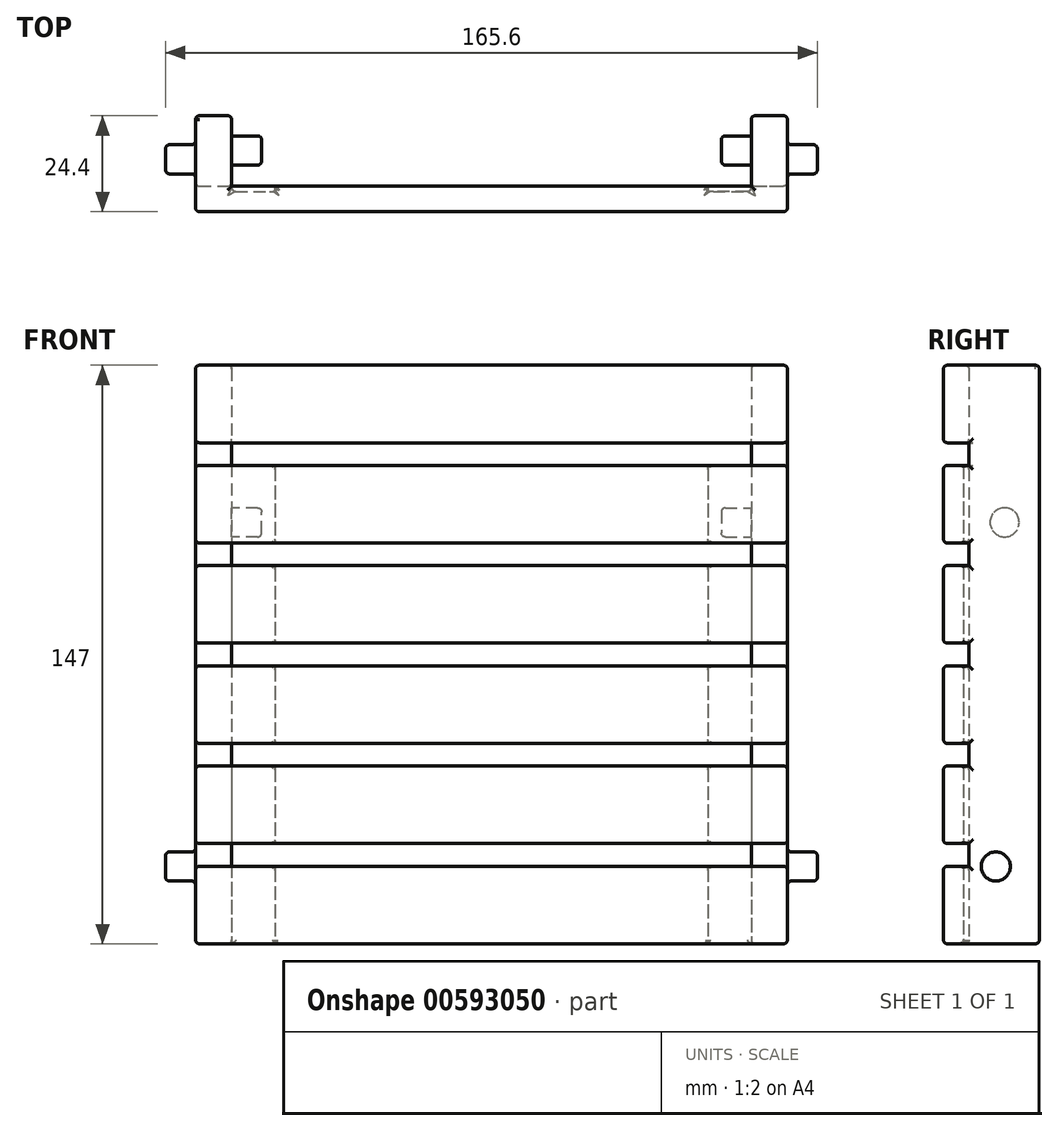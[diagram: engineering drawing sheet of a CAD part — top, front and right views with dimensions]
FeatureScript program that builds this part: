
annotation { "Feature Type Name" : "Feature", "Feature Type Description" : "" }
export const myFeature = defineFeature(function(context is Context, id is Id, definition is map)
    precondition{}
    {
        {
            var Q0;
            Q0=qCreatedBy(makeId("Front.planeOp"),FACE);
            var sketch = newSketch(context, id + "F0", { "sketchPlane" : qUnion([Q0])});
            skLineSegment(sketch, "E0.bottom", {"start": v(-75.2, 73.5) * mm, "end": v(-66, 73.5) * mm});
            skLineSegment(sketch, "E0.top", {"start": v(-75.2, -73.5) * mm, "end": v(-66, -73.5) * mm});
            skLineSegment(sketch, "E0.left", {"start": v(-75.2, 73.5) * mm, "end": v(-75.2, -73.5) * mm});
            skLineSegment(sketch, "E0.right", {"start": v(-66, 73.5) * mm, "end": v(-66, -73.5) * mm});
            skLineSegment(sketch, "E1.MirrorCS", {"start": v(75.2, 73.5) * mm, "end": v(66, 73.5) * mm});
            skLineSegment(sketch, "E2.MirrorCS", {"start": v(75.2, -73.5) * mm, "end": v(66, -73.5) * mm});
            skLineSegment(sketch, "E3.MirrorCS", {"start": v(66, 73.5) * mm, "end": v(66, -73.5) * mm});
            skLineSegment(sketch, "E4.MirrorCS", {"start": v(75.2, 73.5) * mm, "end": v(75.2, -73.5) * mm});
            skSolve(sketch);
        }
        {
            var Q0;
            Q0=qSketchRegion(id+"F0",true);
            extrude(context, id + "F1", {"entities" : qUnion([Q0]), "depth" : 17.9 * mm});
        }
        {
            var Q0;
            Q0=makeQuery(id+"F1.opExtrude","CAP_FACE",FACE,{"disambiguationData":[OSD([sQuery(id+"F0.wireOp",EDGE,"E0.bottom"),sQuery(id+"F0.wireOp",EDGE,"E0.top"),sQuery(id+"F0.wireOp",EDGE,"E0.left"),sQuery(id+"F0.wireOp",EDGE,"E0.right")])],"isStart":false});
            var sketch = newSketch(context, id + "F2", { "sketchPlane" : qUnion([Q0])});
            skLineSegment(sketch, "E5.bottom", {"start": v(-75.2, 73.5) * mm, "end": v(75.2, 73.5) * mm});
            skLineSegment(sketch, "E5.top", {"start": v(-75.2, 53.8) * mm, "end": v(75.2, 53.8) * mm});
            skLineSegment(sketch, "E5.left", {"start": v(-75.2, 73.5) * mm, "end": v(-75.2, 53.8) * mm});
            skLineSegment(sketch, "E5.right", {"start": v(75.2, 73.5) * mm, "end": v(75.2, 53.8) * mm});
            skLineSegment(sketch, "E6.bottom", {"start": v(-75.2, 48.04) * mm, "end": v(75.2, 48.04) * mm});
            skLineSegment(sketch, "E6.top", {"start": v(-75.2, 28.34) * mm, "end": v(75.2, 28.34) * mm});
            skLineSegment(sketch, "E6.left", {"start": v(-75.2, 48.04) * mm, "end": v(-75.2, 28.34) * mm});
            skLineSegment(sketch, "E6.right", {"start": v(75.2, 48.04) * mm, "end": v(75.2, 28.34) * mm});
            skLineSegment(sketch, "E7.bottom", {"start": v(-75.2, 22.58) * mm, "end": v(75.2, 22.58) * mm});
            skLineSegment(sketch, "E7.top", {"start": v(-75.2, 2.88) * mm, "end": v(75.2, 2.88) * mm});
            skLineSegment(sketch, "E7.left", {"start": v(-75.2, 22.58) * mm, "end": v(-75.2, 2.88) * mm});
            skLineSegment(sketch, "E7.right", {"start": v(75.2, 22.58) * mm, "end": v(75.2, 2.88) * mm});
            skLineSegment(sketch, "E8.bottom", {"start": v(-75.2, -2.88) * mm, "end": v(75.2, -2.88) * mm});
            skLineSegment(sketch, "E8.top", {"start": v(-75.2, -22.58) * mm, "end": v(75.2, -22.58) * mm});
            skLineSegment(sketch, "E8.left", {"start": v(-75.2, -2.88) * mm, "end": v(-75.2, -22.58) * mm});
            skLineSegment(sketch, "E8.right", {"start": v(75.2, -2.88) * mm, "end": v(75.2, -22.58) * mm});
            skLineSegment(sketch, "E9.bottom", {"start": v(-75.2, -28.34) * mm, "end": v(75.2, -28.34) * mm});
            skLineSegment(sketch, "E9.top", {"start": v(-75.2, -48.04) * mm, "end": v(75.2, -48.04) * mm});
            skLineSegment(sketch, "E9.left", {"start": v(-75.2, -28.34) * mm, "end": v(-75.2, -48.04) * mm});
            skLineSegment(sketch, "E9.right", {"start": v(75.2, -28.34) * mm, "end": v(75.2, -48.04) * mm});
            skLineSegment(sketch, "E10.bottom", {"start": v(-75.2, -53.8) * mm, "end": v(75.2, -53.8) * mm});
            skLineSegment(sketch, "E10.top", {"start": v(-75.2, -73.5) * mm, "end": v(75.2, -73.5) * mm});
            skLineSegment(sketch, "E10.left", {"start": v(-75.2, -53.8) * mm, "end": v(-75.2, -73.5) * mm});
            skLineSegment(sketch, "E10.right", {"start": v(75.2, -53.8) * mm, "end": v(75.2, -73.5) * mm});
            skSolve(sketch);
        }
        {
            var Q0;
            Q0=qSketchRegion(id+"F2",true);
            extrude(context, id + "F3", {"entities" : qUnion([Q0]), "depth" : 6.5 * mm});
        }
        {
            var Q0;
            Q0=makeQuery(id+"F1.opExtrude","SWEPT_BODY",BODY,{"disambiguationData":[OSD([sQuery(id+"F0.wireOp",EDGE,"E0.bottom"),sQuery(id+"F0.wireOp",EDGE,"E0.top"),sQuery(id+"F0.wireOp",EDGE,"E0.left"),sQuery(id+"F0.wireOp",EDGE,"E0.right")])]});
            var Q1;
            Q1=makeQuery(id+"F1.opExtrude","SWEPT_BODY",BODY,{"disambiguationData":[OSD([sQuery(id+"F0.wireOp",EDGE,"E1.MirrorCS"),sQuery(id+"F0.wireOp",EDGE,"E2.MirrorCS"),sQuery(id+"F0.wireOp",EDGE,"E3.MirrorCS"),sQuery(id+"F0.wireOp",EDGE,"E4.MirrorCS")])]});
            var Q2;
            Q2=makeQuery(id+"F3.opExtrude","SWEPT_BODY",BODY,{"disambiguationData":[OSD([sQuery(id+"F2.wireOp",EDGE,"E5.bottom"),sQuery(id+"F2.wireOp",EDGE,"E5.top"),sQuery(id+"F2.wireOp",EDGE,"E5.left"),sQuery(id+"F2.wireOp",EDGE,"E5.right")])]});
            var Q3;
            Q3=makeQuery(id+"F3.opExtrude","SWEPT_BODY",BODY,{"disambiguationData":[OSD([sQuery(id+"F2.wireOp",EDGE,"E6.bottom"),sQuery(id+"F2.wireOp",EDGE,"E6.top"),sQuery(id+"F2.wireOp",EDGE,"E6.left"),sQuery(id+"F2.wireOp",EDGE,"E6.right")])]});
            var Q4;
            Q4=makeQuery(id+"F3.opExtrude","SWEPT_BODY",BODY,{"disambiguationData":[OSD([sQuery(id+"F2.wireOp",EDGE,"E7.bottom"),sQuery(id+"F2.wireOp",EDGE,"E7.top"),sQuery(id+"F2.wireOp",EDGE,"E7.left"),sQuery(id+"F2.wireOp",EDGE,"E7.right")])]});
            var Q5;
            Q5=makeQuery(id+"F3.opExtrude","SWEPT_BODY",BODY,{"disambiguationData":[OSD([sQuery(id+"F2.wireOp",EDGE,"E8.bottom"),sQuery(id+"F2.wireOp",EDGE,"E8.top"),sQuery(id+"F2.wireOp",EDGE,"E8.left"),sQuery(id+"F2.wireOp",EDGE,"E8.right")])]});
            var Q6;
            Q6=makeQuery(id+"F3.opExtrude","SWEPT_BODY",BODY,{"disambiguationData":[OSD([sQuery(id+"F2.wireOp",EDGE,"E9.bottom"),sQuery(id+"F2.wireOp",EDGE,"E9.top"),sQuery(id+"F2.wireOp",EDGE,"E9.left"),sQuery(id+"F2.wireOp",EDGE,"E9.right")])]});
            var Q7;
            Q7=makeQuery(id+"F3.opExtrude","SWEPT_BODY",BODY,{"disambiguationData":[OSD([sQuery(id+"F2.wireOp",EDGE,"E10.bottom"),sQuery(id+"F2.wireOp",EDGE,"E10.top"),sQuery(id+"F2.wireOp",EDGE,"E10.left"),sQuery(id+"F2.wireOp",EDGE,"E10.right")])]});
            booleanBodies(context, id + "F4", {"operationType" : BooleanOperationType.UNION, "tools" : qUnion([Q0, Q1, Q2, Q3, Q4, Q5, Q6, Q7])});
        }
        {
            var Q0;
            Q0=makeQuery(id+"F4.opBoolean","MERGE",FACE,{"derivedFrom":[makeQuery(id+"F1.opExtrude","SWEPT_FACE",FACE,{"disambiguationData":[OSD([sQuery(id+"F0.wireOp",EDGE,"E0.left")])]}),makeQuery(id+"F3.opExtrude","SWEPT_FACE",FACE,{"disambiguationData":[OSD([sQuery(id+"F2.wireOp",EDGE,"E5.left")])]}),makeQuery(id+"F3.opExtrude","SWEPT_FACE",FACE,{"disambiguationData":[OSD([sQuery(id+"F2.wireOp",EDGE,"E6.left")])]}),makeQuery(id+"F3.opExtrude","SWEPT_FACE",FACE,{"disambiguationData":[OSD([sQuery(id+"F2.wireOp",EDGE,"E7.left")])]}),makeQuery(id+"F3.opExtrude","SWEPT_FACE",FACE,{"disambiguationData":[OSD([sQuery(id+"F2.wireOp",EDGE,"E8.left")])]}),makeQuery(id+"F3.opExtrude","SWEPT_FACE",FACE,{"disambiguationData":[OSD([sQuery(id+"F2.wireOp",EDGE,"E9.left")])]}),makeQuery(id+"F3.opExtrude","SWEPT_FACE",FACE,{"disambiguationData":[OSD([sQuery(id+"F2.wireOp",EDGE,"E10.left")])]})]});
            var sketch = newSketch(context, id + "F5", { "sketchPlane" : qUnion([Q0])});
            skCircle(sketch, "E11", {"center": v(11.08, -53.85) * mm, "radius": 3.7 * mm});
            skSolve(sketch);
        }
        {
            var Q0;
            Q0=makeQuery(id+"F5.imprint","IMPRINT",FACE,{"disambiguationData":[TD([[makeQuery(id+"F5.imprint","IMPRINT",EDGE,{"derivedFrom":sQuery(id+"F5.wireOp",EDGE,"E11")}),1.0]])]});
            extrude(context, id + "F6", {"entities" : qUnion([Q0]), "operationType" : NewBodyOperationType.ADD, "depth" : 7.6 * mm});
        }
        {
            var Q0;
            Q0=makeQuery(id+"F4.opBoolean","MERGE",FACE,{"derivedFrom":[makeQuery(id+"F1.opExtrude","SWEPT_FACE",FACE,{"disambiguationData":[OSD([sQuery(id+"F0.wireOp",EDGE,"E4.MirrorCS")])]}),makeQuery(id+"F3.opExtrude","SWEPT_FACE",FACE,{"disambiguationData":[OSD([sQuery(id+"F2.wireOp",EDGE,"E5.right")])]}),makeQuery(id+"F3.opExtrude","SWEPT_FACE",FACE,{"disambiguationData":[OSD([sQuery(id+"F2.wireOp",EDGE,"E6.right")])]}),makeQuery(id+"F3.opExtrude","SWEPT_FACE",FACE,{"disambiguationData":[OSD([sQuery(id+"F2.wireOp",EDGE,"E7.right")])]}),makeQuery(id+"F3.opExtrude","SWEPT_FACE",FACE,{"disambiguationData":[OSD([sQuery(id+"F2.wireOp",EDGE,"E8.right")])]}),makeQuery(id+"F3.opExtrude","SWEPT_FACE",FACE,{"disambiguationData":[OSD([sQuery(id+"F2.wireOp",EDGE,"E9.right")])]}),makeQuery(id+"F3.opExtrude","SWEPT_FACE",FACE,{"disambiguationData":[OSD([sQuery(id+"F2.wireOp",EDGE,"E10.right")])]})]});
            var sketch = newSketch(context, id + "F7", { "sketchPlane" : qUnion([Q0])});
            skCircle(sketch, "E12", {"center": v(-11.08, -53.85) * mm, "radius": 3.7 * mm});
            skSolve(sketch);
        }
        {
            var Q0;
            Q0=makeQuery(id+"F7.imprint","IMPRINT",FACE,{"disambiguationData":[TD([[makeQuery(id+"F7.imprint","IMPRINT",EDGE,{"derivedFrom":sQuery(id+"F7.wireOp",EDGE,"E12")}),1.0]])]});
            extrude(context, id + "F8", {"entities" : qUnion([Q0]), "operationType" : NewBodyOperationType.ADD, "depth" : 7.6 * mm});
        }
        {
            var Q0;
            Q0=makeQuery(id+"F1.opExtrude","SWEPT_FACE",FACE,{"disambiguationData":[OSD([sQuery(id+"F0.wireOp",EDGE,"E3.MirrorCS")])]});
            var sketch = newSketch(context, id + "F9", { "sketchPlane" : qUnion([Q0])});
            skCircle(sketch, "E13", {"center": v(8.84, 33.58) * mm, "radius": 3.7 * mm});
            skSolve(sketch);
        }
        {
            var Q0;
            Q0=makeQuery(id+"F9.imprint","IMPRINT",FACE,{"disambiguationData":[TD([[makeQuery(id+"F9.imprint","IMPRINT",EDGE,{"derivedFrom":sQuery(id+"F9.wireOp",EDGE,"E13")}),1.0]])]});
            extrude(context, id + "F10", {"entities" : qUnion([Q0]), "operationType" : NewBodyOperationType.ADD, "depth" : 7.6 * mm});
        }
        {
            var Q0;
            Q0=makeQuery(id+"F1.opExtrude","SWEPT_FACE",FACE,{"disambiguationData":[OSD([sQuery(id+"F0.wireOp",EDGE,"E0.right")])]});
            var sketch = newSketch(context, id + "F11", { "sketchPlane" : qUnion([Q0])});
            skCircle(sketch, "E14", {"center": v(-8.84, 33.58) * mm, "radius": 3.7 * mm});
            skSolve(sketch);
        }
        {
            var Q0;
            Q0=makeQuery(id+"F11.imprint","IMPRINT",FACE,{"disambiguationData":[TD([[makeQuery(id+"F11.imprint","IMPRINT",EDGE,{"derivedFrom":sQuery(id+"F11.wireOp",EDGE,"E14")}),1.0]])]});
            extrude(context, id + "F12", {"entities" : qUnion([Q0]), "operationType" : NewBodyOperationType.ADD, "depth" : 7.6 * mm});
        }
        {
            var Q0;
            Q0=makeQuery(id+"F3.opExtrude","CAP_FACE",FACE,{"disambiguationData":[OSD([sQuery(id+"F2.wireOp",EDGE,"E6.bottom"),sQuery(id+"F2.wireOp",EDGE,"E6.top"),sQuery(id+"F2.wireOp",EDGE,"E6.left"),sQuery(id+"F2.wireOp",EDGE,"E6.right")])],"isStart":true});
            var sketch = newSketch(context, id + "F13", { "sketchPlane" : qUnion([Q0])});
            skLineSegment(sketch, "E15.bottom", {"start": v(-66, 48.04) * mm, "end": v(-55, 48.04) * mm});
            skLineSegment(sketch, "E15.top", {"start": v(-66, -73.5) * mm, "end": v(-55, -73.5) * mm});
            skLineSegment(sketch, "E15.left", {"start": v(-66, 48.04) * mm, "end": v(-66, -73.5) * mm});
            skLineSegment(sketch, "E15.right", {"start": v(-55, 48.04) * mm, "end": v(-55, -73.5) * mm});
            skLineSegment(sketch, "E16.bottom", {"start": v(66, 48.04) * mm, "end": v(55, 48.04) * mm});
            skLineSegment(sketch, "E16.top", {"start": v(66, -73.5) * mm, "end": v(55, -73.5) * mm});
            skLineSegment(sketch, "E16.left", {"start": v(66, 48.04) * mm, "end": v(66, -73.5) * mm});
            skLineSegment(sketch, "E16.right", {"start": v(55, 48.04) * mm, "end": v(55, -73.5) * mm});
            skSolve(sketch);
        }
        {
            var Q0;
            {var subQ0=sQuery(id+"F13.wireOp",EDGE,"E15.top");Q0=makeQuery(id+"F13.imprint","IMPRINT",FACE,{"disambiguationData":[TD([[makeQuery(id+"F13.imprint","IMPRINT",EDGE,{"derivedFrom":subQ0}),1.0]])]});}
            var Q1;
            {var subQ0=sQuery(id+"F13.wireOp",EDGE,"E15.bottom");Q1=makeQuery(id+"F13.imprint","IMPRINT",FACE,{"disambiguationData":[TD([[makeQuery(id+"F13.imprint","IMPRINT",EDGE,{"derivedFrom":subQ0}),1.0]])]});}
            var Q2;
            {var subQ0=sQuery(id+"F13.wireOp",EDGE,"E16.bottom");Q2=makeQuery(id+"F13.imprint","IMPRINT",FACE,{"disambiguationData":[TD([[makeQuery(id+"F13.imprint","IMPRINT",EDGE,{"derivedFrom":subQ0}),1.0]])]});}
            var Q3;
            {var subQ0=sQuery(id+"F13.wireOp",EDGE,"E16.top");Q3=makeQuery(id+"F13.imprint","IMPRINT",FACE,{"disambiguationData":[TD([[makeQuery(id+"F13.imprint","IMPRINT",EDGE,{"derivedFrom":subQ0}),-1.0]])]});}
            extrude(context, id + "F14", {"entities" : qUnion([Q0, Q1, Q2, Q3]), "operationType" : NewBodyOperationType.REMOVE, "oppositeDirection" : true, "depth" : 1.35 * mm});
        }
        {
            var Q0;
            Q0=makeQuery(id+"F3.opExtrude","CAP_FACE",FACE,{"disambiguationData":[OSD([sQuery(id+"F2.wireOp",EDGE,"E10.bottom"),sQuery(id+"F2.wireOp",EDGE,"E10.top"),sQuery(id+"F2.wireOp",EDGE,"E10.left"),sQuery(id+"F2.wireOp",EDGE,"E10.right")])],"isStart":false});
            var Q1;
            Q1=makeQuery(id+"F3.opExtrude","CAP_FACE",FACE,{"disambiguationData":[OSD([sQuery(id+"F2.wireOp",EDGE,"E9.bottom"),sQuery(id+"F2.wireOp",EDGE,"E9.top"),sQuery(id+"F2.wireOp",EDGE,"E9.left"),sQuery(id+"F2.wireOp",EDGE,"E9.right")])],"isStart":false});
            var Q2;
            Q2=makeQuery(id+"F3.opExtrude","CAP_FACE",FACE,{"disambiguationData":[OSD([sQuery(id+"F2.wireOp",EDGE,"E8.bottom"),sQuery(id+"F2.wireOp",EDGE,"E8.top"),sQuery(id+"F2.wireOp",EDGE,"E8.left"),sQuery(id+"F2.wireOp",EDGE,"E8.right")])],"isStart":false});
            var Q3;
            Q3=makeQuery(id+"F3.opExtrude","CAP_FACE",FACE,{"disambiguationData":[OSD([sQuery(id+"F2.wireOp",EDGE,"E7.bottom"),sQuery(id+"F2.wireOp",EDGE,"E7.top"),sQuery(id+"F2.wireOp",EDGE,"E7.left"),sQuery(id+"F2.wireOp",EDGE,"E7.right")])],"isStart":false});
            var Q4;
            Q4=makeQuery(id+"F3.opExtrude","CAP_FACE",FACE,{"disambiguationData":[OSD([sQuery(id+"F2.wireOp",EDGE,"E6.bottom"),sQuery(id+"F2.wireOp",EDGE,"E6.top"),sQuery(id+"F2.wireOp",EDGE,"E6.left"),sQuery(id+"F2.wireOp",EDGE,"E6.right")])],"isStart":false});
            var Q5;
            Q5=makeQuery(id+"F3.opExtrude","CAP_FACE",FACE,{"disambiguationData":[OSD([sQuery(id+"F2.wireOp",EDGE,"E5.bottom"),sQuery(id+"F2.wireOp",EDGE,"E5.top"),sQuery(id+"F2.wireOp",EDGE,"E5.left"),sQuery(id+"F2.wireOp",EDGE,"E5.right")])],"isStart":false});
            var Q6;
            Q6=makeQuery(id+"F4.opBoolean","MERGE",FACE,{"derivedFrom":[makeQuery(id+"F1.opExtrude","SWEPT_FACE",FACE,{"disambiguationData":[OSD([sQuery(id+"F0.wireOp",EDGE,"E4.MirrorCS")])]}),makeQuery(id+"F3.opExtrude","SWEPT_FACE",FACE,{"disambiguationData":[OSD([sQuery(id+"F2.wireOp",EDGE,"E5.right")])]}),makeQuery(id+"F3.opExtrude","SWEPT_FACE",FACE,{"disambiguationData":[OSD([sQuery(id+"F2.wireOp",EDGE,"E6.right")])]}),makeQuery(id+"F3.opExtrude","SWEPT_FACE",FACE,{"disambiguationData":[OSD([sQuery(id+"F2.wireOp",EDGE,"E7.right")])]}),makeQuery(id+"F3.opExtrude","SWEPT_FACE",FACE,{"disambiguationData":[OSD([sQuery(id+"F2.wireOp",EDGE,"E8.right")])]}),makeQuery(id+"F3.opExtrude","SWEPT_FACE",FACE,{"disambiguationData":[OSD([sQuery(id+"F2.wireOp",EDGE,"E9.right")])]}),makeQuery(id+"F3.opExtrude","SWEPT_FACE",FACE,{"disambiguationData":[OSD([sQuery(id+"F2.wireOp",EDGE,"E10.right")])]})]});
            var Q7;
            Q7=makeQuery(id+"F4.opBoolean","MERGE",FACE,{"derivedFrom":[makeQuery(id+"F1.opExtrude","SWEPT_FACE",FACE,{"disambiguationData":[OSD([sQuery(id+"F0.wireOp",EDGE,"E0.left")])]}),makeQuery(id+"F3.opExtrude","SWEPT_FACE",FACE,{"disambiguationData":[OSD([sQuery(id+"F2.wireOp",EDGE,"E5.left")])]}),makeQuery(id+"F3.opExtrude","SWEPT_FACE",FACE,{"disambiguationData":[OSD([sQuery(id+"F2.wireOp",EDGE,"E6.left")])]}),makeQuery(id+"F3.opExtrude","SWEPT_FACE",FACE,{"disambiguationData":[OSD([sQuery(id+"F2.wireOp",EDGE,"E7.left")])]}),makeQuery(id+"F3.opExtrude","SWEPT_FACE",FACE,{"disambiguationData":[OSD([sQuery(id+"F2.wireOp",EDGE,"E8.left")])]}),makeQuery(id+"F3.opExtrude","SWEPT_FACE",FACE,{"disambiguationData":[OSD([sQuery(id+"F2.wireOp",EDGE,"E9.left")])]}),makeQuery(id+"F3.opExtrude","SWEPT_FACE",FACE,{"disambiguationData":[OSD([sQuery(id+"F2.wireOp",EDGE,"E10.left")])]})]});
            var Q8;
            Q8=makeQuery(id+"F4.opBoolean","MERGE",FACE,{"derivedFrom":[makeQuery(id+"F1.opExtrude","SWEPT_FACE",FACE,{"disambiguationData":[OSD([sQuery(id+"F0.wireOp",EDGE,"E0.top")])]}),makeQuery(id+"F1.opExtrude","SWEPT_FACE",FACE,{"disambiguationData":[OSD([sQuery(id+"F0.wireOp",EDGE,"E2.MirrorCS")])]}),makeQuery(id+"F3.opExtrude","SWEPT_FACE",FACE,{"disambiguationData":[OSD([sQuery(id+"F2.wireOp",EDGE,"E10.top")])]})]});
            var Q9;
            Q9=makeQuery(id+"F4.opBoolean","MERGE",FACE,{"derivedFrom":[makeQuery(id+"F1.opExtrude","SWEPT_FACE",FACE,{"disambiguationData":[OSD([sQuery(id+"F0.wireOp",EDGE,"E0.bottom")])]}),makeQuery(id+"F1.opExtrude","SWEPT_FACE",FACE,{"disambiguationData":[OSD([sQuery(id+"F0.wireOp",EDGE,"E1.MirrorCS")])]}),makeQuery(id+"F3.opExtrude","SWEPT_FACE",FACE,{"disambiguationData":[OSD([sQuery(id+"F2.wireOp",EDGE,"E5.bottom")])]})]});
            fillet(context, id + "F15", {"entities" : qUnion([Q0, Q1, Q2, Q3, Q4, Q5, Q6, Q7, Q8, Q9]), "radius" : 1 * mm, "tangentPropagation" : true, "allowEdgeOverflow" : false});
        }
        {
            var Q0;
            {var subQ0=sQuery(id+"F13.wireOp",EDGE,"E15.left");Q0=makeQuery(id+"F14.boolean.opBoolean","COPY",EDGE,{"disambiguationData":[TD([makeQuery(id+"F1.opExtrude","SWEPT_FACE",FACE,{"disambiguationData":[OSD([sQuery(id+"F0.wireOp",EDGE,"E0.top")])]})])],"derivedFrom":makeQuery(id+"F14.opExtrude","CAP_EDGE",EDGE,{"disambiguationData":[OSD([subQ0])],"isStart":false})});}
            var Q1;
            {var subQ0=sQuery(id+"F13.wireOp",EDGE,"E15.left");Q1=makeQuery(id+"F14.boolean.opBoolean","COPY",EDGE,{"disambiguationData":[TD([makeQuery(id+"F3.opExtrude","SWEPT_FACE",FACE,{"disambiguationData":[OSD([sQuery(id+"F2.wireOp",EDGE,"E9.bottom")])]})])],"derivedFrom":makeQuery(id+"F14.opExtrude","CAP_EDGE",EDGE,{"disambiguationData":[OSD([subQ0])],"isStart":false})});}
            var Q2;
            {var subQ0=sQuery(id+"F13.wireOp",EDGE,"E15.left");Q2=makeQuery(id+"F14.boolean.opBoolean","COPY",EDGE,{"disambiguationData":[TD([makeQuery(id+"F3.opExtrude","SWEPT_FACE",FACE,{"disambiguationData":[OSD([sQuery(id+"F2.wireOp",EDGE,"E8.bottom")])]})])],"derivedFrom":makeQuery(id+"F14.opExtrude","CAP_EDGE",EDGE,{"disambiguationData":[OSD([subQ0])],"isStart":false})});}
            var Q3;
            {var subQ0=sQuery(id+"F13.wireOp",EDGE,"E15.left");Q3=makeQuery(id+"F14.boolean.opBoolean","COPY",EDGE,{"disambiguationData":[TD([makeQuery(id+"F3.opExtrude","SWEPT_FACE",FACE,{"disambiguationData":[OSD([sQuery(id+"F2.wireOp",EDGE,"E7.bottom")])]})])],"derivedFrom":makeQuery(id+"F14.opExtrude","CAP_EDGE",EDGE,{"disambiguationData":[OSD([subQ0])],"isStart":false})});}
            var Q4;
            {var subQ0=sQuery(id+"F0.wireOp",EDGE,"E3.MirrorCS");var subQ1=sQuery(id+"F0.wireOp",EDGE,"E1.MirrorCS");var subQ2=sQuery(id+"F2.wireOp",EDGE,"E5.bottom");var subQ3=sQuery(id+"F2.wireOp",EDGE,"E5.top");Q4=makeQuery(id+"F4.opBoolean","SPLIT",EDGE,{"disambiguationData":[TD([makeQuery(id+"F1.opExtrude","SWEPT_FACE",FACE,{"disambiguationData":[OSD([sQuery(id+"F0.wireOp",EDGE,"E0.bottom")])]}),makeQuery(id+"F1.opExtrude","SWEPT_FACE",FACE,{"disambiguationData":[OSD([subQ1])]}),makeQuery(id+"F1.opExtrude","CAP_FACE",FACE,{"disambiguationData":[OSD([subQ1,sQuery(id+"F0.wireOp",EDGE,"E2.MirrorCS"),subQ0,sQuery(id+"F0.wireOp",EDGE,"E4.MirrorCS")])],"isStart":false}),makeQuery(id+"F1.opExtrude","SWEPT_FACE",FACE,{"disambiguationData":[OSD([subQ0])]}),makeQuery(id+"F3.opExtrude","SWEPT_FACE",FACE,{"disambiguationData":[OSD([subQ2])]}),makeQuery(id+"F3.opExtrude","CAP_FACE",FACE,{"disambiguationData":[OSD([subQ2,subQ3,sQuery(id+"F2.wireOp",EDGE,"E5.left"),sQuery(id+"F2.wireOp",EDGE,"E5.right")])],"isStart":true}),makeQuery(id+"F3.opExtrude","SWEPT_FACE",FACE,{"disambiguationData":[OSD([subQ3])]})])],"derivedFrom":makeQuery(id+"F1.opExtrude","CAP_EDGE",EDGE,{"disambiguationData":[OSD([subQ0])],"isStart":false})});}
            var Q5;
            {var subQ0=sQuery(id+"F13.wireOp",EDGE,"E15.left");Q5=makeQuery(id+"F14.boolean.opBoolean","COPY",EDGE,{"disambiguationData":[TD([makeQuery(id+"F3.opExtrude","SWEPT_FACE",FACE,{"disambiguationData":[OSD([sQuery(id+"F2.wireOp",EDGE,"E6.bottom")])]})])],"derivedFrom":makeQuery(id+"F14.opExtrude","CAP_EDGE",EDGE,{"disambiguationData":[OSD([subQ0])],"isStart":false})});}
            var Q6;
            Q6=makeQuery(id+"F10.opExtrude","CAP_EDGE",EDGE,{"disambiguationData":[OSD([sQuery(id+"F9.wireOp",EDGE,"E13")])],"isStart":true});
            var Q7;
            Q7=makeQuery(id+"F10.opExtrude","CAP_EDGE",EDGE,{"disambiguationData":[OSD([sQuery(id+"F9.wireOp",EDGE,"E13")])],"isStart":false});
            var Q8;
            Q8=makeQuery(id+"F1.opExtrude","CAP_EDGE",EDGE,{"disambiguationData":[OSD([sQuery(id+"F0.wireOp",EDGE,"E3.MirrorCS")])],"isStart":true});
            var Q9;
            Q9=makeQuery(id+"F1.opExtrude","CAP_EDGE",EDGE,{"disambiguationData":[OSD([sQuery(id+"F0.wireOp",EDGE,"E0.right")])],"isStart":true});
            var Q10;
            Q10=makeQuery(id+"F12.opExtrude","CAP_EDGE",EDGE,{"disambiguationData":[OSD([sQuery(id+"F11.wireOp",EDGE,"E14")])],"isStart":true});
            var Q11;
            Q11=makeQuery(id+"F12.opExtrude","CAP_EDGE",EDGE,{"disambiguationData":[OSD([sQuery(id+"F11.wireOp",EDGE,"E14")])],"isStart":false});
            var Q12;
            {var subQ0=sQuery(id+"F0.wireOp",EDGE,"E0.right");var subQ1=sQuery(id+"F2.wireOp",EDGE,"E5.bottom");var subQ2=sQuery(id+"F0.wireOp",EDGE,"E0.bottom");var subQ3=sQuery(id+"F2.wireOp",EDGE,"E5.top");Q12=makeQuery(id+"F4.opBoolean","SPLIT",EDGE,{"disambiguationData":[TD([makeQuery(id+"F1.opExtrude","SWEPT_FACE",FACE,{"disambiguationData":[OSD([subQ2])]}),makeQuery(id+"F1.opExtrude","CAP_FACE",FACE,{"disambiguationData":[OSD([subQ2,sQuery(id+"F0.wireOp",EDGE,"E0.top"),sQuery(id+"F0.wireOp",EDGE,"E0.left"),subQ0])],"isStart":false}),makeQuery(id+"F1.opExtrude","SWEPT_FACE",FACE,{"disambiguationData":[OSD([subQ0])]}),makeQuery(id+"F1.opExtrude","SWEPT_FACE",FACE,{"disambiguationData":[OSD([sQuery(id+"F0.wireOp",EDGE,"E1.MirrorCS")])]}),makeQuery(id+"F3.opExtrude","SWEPT_FACE",FACE,{"disambiguationData":[OSD([subQ1])]}),makeQuery(id+"F3.opExtrude","CAP_FACE",FACE,{"disambiguationData":[OSD([subQ1,subQ3,sQuery(id+"F2.wireOp",EDGE,"E5.left"),sQuery(id+"F2.wireOp",EDGE,"E5.right")])],"isStart":true}),makeQuery(id+"F3.opExtrude","SWEPT_FACE",FACE,{"disambiguationData":[OSD([subQ3])]})])],"derivedFrom":makeQuery(id+"F1.opExtrude","CAP_EDGE",EDGE,{"disambiguationData":[OSD([subQ0])],"isStart":false})});}
            var Q13;
            {var subQ0=sQuery(id+"F13.wireOp",EDGE,"E16.left");Q13=makeQuery(id+"F14.boolean.opBoolean","COPY",EDGE,{"disambiguationData":[TD([makeQuery(id+"F3.opExtrude","SWEPT_FACE",FACE,{"disambiguationData":[OSD([sQuery(id+"F2.wireOp",EDGE,"E6.bottom")])]})])],"derivedFrom":makeQuery(id+"F14.opExtrude","CAP_EDGE",EDGE,{"disambiguationData":[OSD([subQ0])],"isStart":false})});}
            var Q14;
            {var subQ0=sQuery(id+"F13.wireOp",EDGE,"E16.left");Q14=makeQuery(id+"F14.boolean.opBoolean","COPY",EDGE,{"disambiguationData":[TD([makeQuery(id+"F3.opExtrude","SWEPT_FACE",FACE,{"disambiguationData":[OSD([sQuery(id+"F2.wireOp",EDGE,"E7.bottom")])]})])],"derivedFrom":makeQuery(id+"F14.opExtrude","CAP_EDGE",EDGE,{"disambiguationData":[OSD([subQ0])],"isStart":false})});}
            var Q15;
            {var subQ0=sQuery(id+"F13.wireOp",EDGE,"E16.left");Q15=makeQuery(id+"F14.boolean.opBoolean","COPY",EDGE,{"disambiguationData":[TD([makeQuery(id+"F3.opExtrude","SWEPT_FACE",FACE,{"disambiguationData":[OSD([sQuery(id+"F2.wireOp",EDGE,"E8.bottom")])]})])],"derivedFrom":makeQuery(id+"F14.opExtrude","CAP_EDGE",EDGE,{"disambiguationData":[OSD([subQ0])],"isStart":false})});}
            var Q16;
            {var subQ0=sQuery(id+"F13.wireOp",EDGE,"E16.left");Q16=makeQuery(id+"F14.boolean.opBoolean","COPY",EDGE,{"disambiguationData":[TD([makeQuery(id+"F3.opExtrude","SWEPT_FACE",FACE,{"disambiguationData":[OSD([sQuery(id+"F2.wireOp",EDGE,"E9.bottom")])]})])],"derivedFrom":makeQuery(id+"F14.opExtrude","CAP_EDGE",EDGE,{"disambiguationData":[OSD([subQ0])],"isStart":false})});}
            var Q17;
            {var subQ0=sQuery(id+"F13.wireOp",EDGE,"E16.left");Q17=makeQuery(id+"F14.boolean.opBoolean","COPY",EDGE,{"disambiguationData":[TD([makeQuery(id+"F1.opExtrude","SWEPT_FACE",FACE,{"disambiguationData":[OSD([sQuery(id+"F0.wireOp",EDGE,"E0.top")])]})])],"derivedFrom":makeQuery(id+"F14.opExtrude","CAP_EDGE",EDGE,{"disambiguationData":[OSD([subQ0])],"isStart":false})});}
            var Q18;
            Q18=makeQuery(id+"F6.opExtrude","CAP_FACE",FACE,{"disambiguationData":[OSD([sQuery(id+"F5.wireOp",EDGE,"E11")])],"isStart":false});
            var Q19;
            Q19=makeQuery(id+"F8.opExtrude","CAP_FACE",FACE,{"disambiguationData":[OSD([sQuery(id+"F7.wireOp",EDGE,"E12")])],"isStart":false});
            fillet(context, id + "F16", {"entities" : qUnion([Q0, Q1, Q2, Q3, Q4, Q5, Q6, Q7, Q8, Q9, Q10, Q11, Q12, Q13, Q14, Q15, Q16, Q17, Q18, Q19]), "radius" : 1 * mm, "tangentPropagation" : true, "allowEdgeOverflow" : false});
        }
        {
            var Q0;
            {var subQ0=sQuery(id+"F2.wireOp",EDGE,"E9.right");var subQ1=sQuery(id+"F2.wireOp",EDGE,"E9.top");var subQ2=sQuery(id+"F0.wireOp",EDGE,"E3.MirrorCS");var subQ3=sQuery(id+"F0.wireOp",EDGE,"E4.MirrorCS");Q0=makeQuery(id+"F4.opBoolean","SPLIT",EDGE,{"disambiguationData":[TD([makeQuery(id+"F1.opExtrude","CAP_FACE",FACE,{"disambiguationData":[OSD([sQuery(id+"F0.wireOp",EDGE,"E1.MirrorCS"),sQuery(id+"F0.wireOp",EDGE,"E2.MirrorCS"),subQ2,subQ3])],"isStart":false}),makeQuery(id+"F1.opExtrude","SWEPT_FACE",FACE,{"disambiguationData":[OSD([subQ2])]}),makeQuery(id+"F1.opExtrude","SWEPT_FACE",FACE,{"disambiguationData":[OSD([subQ3])]}),makeQuery(id+"F3.opExtrude","SWEPT_FACE",FACE,{"disambiguationData":[OSD([sQuery(id+"F2.wireOp",EDGE,"E5.right")])]}),makeQuery(id+"F3.opExtrude","SWEPT_FACE",FACE,{"disambiguationData":[OSD([sQuery(id+"F2.wireOp",EDGE,"E6.right")])]}),makeQuery(id+"F3.opExtrude","SWEPT_FACE",FACE,{"disambiguationData":[OSD([sQuery(id+"F2.wireOp",EDGE,"E7.right")])]}),makeQuery(id+"F3.opExtrude","SWEPT_FACE",FACE,{"disambiguationData":[OSD([sQuery(id+"F2.wireOp",EDGE,"E8.right")])]}),makeQuery(id+"F3.opExtrude","CAP_FACE",FACE,{"disambiguationData":[OSD([sQuery(id+"F2.wireOp",EDGE,"E9.bottom"),subQ1,sQuery(id+"F2.wireOp",EDGE,"E9.left"),subQ0])],"isStart":true}),makeQuery(id+"F3.opExtrude","SWEPT_FACE",FACE,{"disambiguationData":[OSD([subQ1])]}),makeQuery(id+"F3.opExtrude","SWEPT_FACE",FACE,{"disambiguationData":[OSD([subQ0])]}),makeQuery(id+"F3.opExtrude","SWEPT_FACE",FACE,{"disambiguationData":[OSD([sQuery(id+"F2.wireOp",EDGE,"E10.right")])]})])],"derivedFrom":makeQuery(id+"F3.opExtrude","CAP_EDGE",EDGE,{"disambiguationData":[OSD([subQ1])],"isStart":true})});}
            var Q1;
            {var subQ0=sQuery(id+"F2.wireOp",EDGE,"E10.bottom");var subQ1=sQuery(id+"F0.wireOp",EDGE,"E3.MirrorCS");var subQ2=sQuery(id+"F0.wireOp",EDGE,"E4.MirrorCS");var subQ3=sQuery(id+"F2.wireOp",EDGE,"E10.right");Q1=makeQuery(id+"F4.opBoolean","SPLIT",EDGE,{"disambiguationData":[TD([makeQuery(id+"F1.opExtrude","CAP_FACE",FACE,{"disambiguationData":[OSD([sQuery(id+"F0.wireOp",EDGE,"E1.MirrorCS"),sQuery(id+"F0.wireOp",EDGE,"E2.MirrorCS"),subQ1,subQ2])],"isStart":false}),makeQuery(id+"F1.opExtrude","SWEPT_FACE",FACE,{"disambiguationData":[OSD([subQ1])]}),makeQuery(id+"F1.opExtrude","SWEPT_FACE",FACE,{"disambiguationData":[OSD([subQ2])]}),makeQuery(id+"F3.opExtrude","SWEPT_FACE",FACE,{"disambiguationData":[OSD([sQuery(id+"F2.wireOp",EDGE,"E5.right")])]}),makeQuery(id+"F3.opExtrude","SWEPT_FACE",FACE,{"disambiguationData":[OSD([sQuery(id+"F2.wireOp",EDGE,"E6.right")])]}),makeQuery(id+"F3.opExtrude","SWEPT_FACE",FACE,{"disambiguationData":[OSD([sQuery(id+"F2.wireOp",EDGE,"E7.right")])]}),makeQuery(id+"F3.opExtrude","SWEPT_FACE",FACE,{"disambiguationData":[OSD([sQuery(id+"F2.wireOp",EDGE,"E8.right")])]}),makeQuery(id+"F3.opExtrude","SWEPT_FACE",FACE,{"disambiguationData":[OSD([sQuery(id+"F2.wireOp",EDGE,"E9.right")])]}),makeQuery(id+"F3.opExtrude","SWEPT_FACE",FACE,{"disambiguationData":[OSD([subQ0])]}),makeQuery(id+"F3.opExtrude","CAP_FACE",FACE,{"disambiguationData":[OSD([subQ0,sQuery(id+"F2.wireOp",EDGE,"E10.top"),sQuery(id+"F2.wireOp",EDGE,"E10.left"),subQ3])],"isStart":true}),makeQuery(id+"F3.opExtrude","SWEPT_FACE",FACE,{"disambiguationData":[OSD([subQ3])]})])],"derivedFrom":makeQuery(id+"F3.opExtrude","CAP_EDGE",EDGE,{"disambiguationData":[OSD([subQ0])],"isStart":true})});}
            var Q2;
            {var subQ0=sQuery(id+"F2.wireOp",EDGE,"E9.right");var subQ1=sQuery(id+"F2.wireOp",EDGE,"E9.bottom");var subQ2=sQuery(id+"F0.wireOp",EDGE,"E3.MirrorCS");var subQ3=sQuery(id+"F0.wireOp",EDGE,"E4.MirrorCS");Q2=makeQuery(id+"F4.opBoolean","SPLIT",EDGE,{"disambiguationData":[TD([makeQuery(id+"F1.opExtrude","CAP_FACE",FACE,{"disambiguationData":[OSD([sQuery(id+"F0.wireOp",EDGE,"E1.MirrorCS"),sQuery(id+"F0.wireOp",EDGE,"E2.MirrorCS"),subQ2,subQ3])],"isStart":false}),makeQuery(id+"F1.opExtrude","SWEPT_FACE",FACE,{"disambiguationData":[OSD([subQ2])]}),makeQuery(id+"F1.opExtrude","SWEPT_FACE",FACE,{"disambiguationData":[OSD([subQ3])]}),makeQuery(id+"F3.opExtrude","SWEPT_FACE",FACE,{"disambiguationData":[OSD([sQuery(id+"F2.wireOp",EDGE,"E5.right")])]}),makeQuery(id+"F3.opExtrude","SWEPT_FACE",FACE,{"disambiguationData":[OSD([sQuery(id+"F2.wireOp",EDGE,"E6.right")])]}),makeQuery(id+"F3.opExtrude","SWEPT_FACE",FACE,{"disambiguationData":[OSD([sQuery(id+"F2.wireOp",EDGE,"E7.right")])]}),makeQuery(id+"F3.opExtrude","SWEPT_FACE",FACE,{"disambiguationData":[OSD([sQuery(id+"F2.wireOp",EDGE,"E8.right")])]}),makeQuery(id+"F3.opExtrude","SWEPT_FACE",FACE,{"disambiguationData":[OSD([subQ1])]}),makeQuery(id+"F3.opExtrude","CAP_FACE",FACE,{"disambiguationData":[OSD([subQ1,sQuery(id+"F2.wireOp",EDGE,"E9.top"),sQuery(id+"F2.wireOp",EDGE,"E9.left"),subQ0])],"isStart":true}),makeQuery(id+"F3.opExtrude","SWEPT_FACE",FACE,{"disambiguationData":[OSD([subQ0])]}),makeQuery(id+"F3.opExtrude","SWEPT_FACE",FACE,{"disambiguationData":[OSD([sQuery(id+"F2.wireOp",EDGE,"E10.right")])]})])],"derivedFrom":makeQuery(id+"F3.opExtrude","CAP_EDGE",EDGE,{"disambiguationData":[OSD([subQ1])],"isStart":true})});}
            var Q3;
            {var subQ0=sQuery(id+"F2.wireOp",EDGE,"E8.right");var subQ1=sQuery(id+"F2.wireOp",EDGE,"E8.top");var subQ2=sQuery(id+"F0.wireOp",EDGE,"E3.MirrorCS");var subQ3=sQuery(id+"F0.wireOp",EDGE,"E4.MirrorCS");Q3=makeQuery(id+"F4.opBoolean","SPLIT",EDGE,{"disambiguationData":[TD([makeQuery(id+"F1.opExtrude","CAP_FACE",FACE,{"disambiguationData":[OSD([sQuery(id+"F0.wireOp",EDGE,"E1.MirrorCS"),sQuery(id+"F0.wireOp",EDGE,"E2.MirrorCS"),subQ2,subQ3])],"isStart":false}),makeQuery(id+"F1.opExtrude","SWEPT_FACE",FACE,{"disambiguationData":[OSD([subQ2])]}),makeQuery(id+"F1.opExtrude","SWEPT_FACE",FACE,{"disambiguationData":[OSD([subQ3])]}),makeQuery(id+"F3.opExtrude","SWEPT_FACE",FACE,{"disambiguationData":[OSD([sQuery(id+"F2.wireOp",EDGE,"E5.right")])]}),makeQuery(id+"F3.opExtrude","SWEPT_FACE",FACE,{"disambiguationData":[OSD([sQuery(id+"F2.wireOp",EDGE,"E6.right")])]}),makeQuery(id+"F3.opExtrude","SWEPT_FACE",FACE,{"disambiguationData":[OSD([sQuery(id+"F2.wireOp",EDGE,"E7.right")])]}),makeQuery(id+"F3.opExtrude","CAP_FACE",FACE,{"disambiguationData":[OSD([sQuery(id+"F2.wireOp",EDGE,"E8.bottom"),subQ1,sQuery(id+"F2.wireOp",EDGE,"E8.left"),subQ0])],"isStart":true}),makeQuery(id+"F3.opExtrude","SWEPT_FACE",FACE,{"disambiguationData":[OSD([subQ1])]}),makeQuery(id+"F3.opExtrude","SWEPT_FACE",FACE,{"disambiguationData":[OSD([subQ0])]}),makeQuery(id+"F3.opExtrude","SWEPT_FACE",FACE,{"disambiguationData":[OSD([sQuery(id+"F2.wireOp",EDGE,"E9.right")])]}),makeQuery(id+"F3.opExtrude","SWEPT_FACE",FACE,{"disambiguationData":[OSD([sQuery(id+"F2.wireOp",EDGE,"E10.right")])]})])],"derivedFrom":makeQuery(id+"F3.opExtrude","CAP_EDGE",EDGE,{"disambiguationData":[OSD([subQ1])],"isStart":true})});}
            var Q4;
            {var subQ0=sQuery(id+"F2.wireOp",EDGE,"E7.right");var subQ1=sQuery(id+"F2.wireOp",EDGE,"E7.top");var subQ2=sQuery(id+"F0.wireOp",EDGE,"E4.MirrorCS");var subQ3=sQuery(id+"F0.wireOp",EDGE,"E3.MirrorCS");Q4=makeQuery(id+"F4.opBoolean","SPLIT",EDGE,{"disambiguationData":[TD([makeQuery(id+"F1.opExtrude","CAP_FACE",FACE,{"disambiguationData":[OSD([sQuery(id+"F0.wireOp",EDGE,"E1.MirrorCS"),sQuery(id+"F0.wireOp",EDGE,"E2.MirrorCS"),subQ3,subQ2])],"isStart":false}),makeQuery(id+"F1.opExtrude","SWEPT_FACE",FACE,{"disambiguationData":[OSD([subQ3])]}),makeQuery(id+"F1.opExtrude","SWEPT_FACE",FACE,{"disambiguationData":[OSD([subQ2])]}),makeQuery(id+"F3.opExtrude","SWEPT_FACE",FACE,{"disambiguationData":[OSD([sQuery(id+"F2.wireOp",EDGE,"E5.right")])]}),makeQuery(id+"F3.opExtrude","SWEPT_FACE",FACE,{"disambiguationData":[OSD([sQuery(id+"F2.wireOp",EDGE,"E6.right")])]}),makeQuery(id+"F3.opExtrude","CAP_FACE",FACE,{"disambiguationData":[OSD([sQuery(id+"F2.wireOp",EDGE,"E7.bottom"),subQ1,sQuery(id+"F2.wireOp",EDGE,"E7.left"),subQ0])],"isStart":true}),makeQuery(id+"F3.opExtrude","SWEPT_FACE",FACE,{"disambiguationData":[OSD([subQ1])]}),makeQuery(id+"F3.opExtrude","SWEPT_FACE",FACE,{"disambiguationData":[OSD([subQ0])]}),makeQuery(id+"F3.opExtrude","SWEPT_FACE",FACE,{"disambiguationData":[OSD([sQuery(id+"F2.wireOp",EDGE,"E8.right")])]}),makeQuery(id+"F3.opExtrude","SWEPT_FACE",FACE,{"disambiguationData":[OSD([sQuery(id+"F2.wireOp",EDGE,"E9.right")])]}),makeQuery(id+"F3.opExtrude","SWEPT_FACE",FACE,{"disambiguationData":[OSD([sQuery(id+"F2.wireOp",EDGE,"E10.right")])]})])],"derivedFrom":makeQuery(id+"F3.opExtrude","CAP_EDGE",EDGE,{"disambiguationData":[OSD([subQ1])],"isStart":true})});}
            var Q5;
            {var subQ0=sQuery(id+"F2.wireOp",EDGE,"E6.right");var subQ1=sQuery(id+"F2.wireOp",EDGE,"E6.top");var subQ2=sQuery(id+"F0.wireOp",EDGE,"E3.MirrorCS");var subQ3=sQuery(id+"F0.wireOp",EDGE,"E4.MirrorCS");Q5=makeQuery(id+"F4.opBoolean","SPLIT",EDGE,{"disambiguationData":[TD([makeQuery(id+"F1.opExtrude","CAP_FACE",FACE,{"disambiguationData":[OSD([sQuery(id+"F0.wireOp",EDGE,"E1.MirrorCS"),sQuery(id+"F0.wireOp",EDGE,"E2.MirrorCS"),subQ2,subQ3])],"isStart":false}),makeQuery(id+"F1.opExtrude","SWEPT_FACE",FACE,{"disambiguationData":[OSD([subQ2])]}),makeQuery(id+"F1.opExtrude","SWEPT_FACE",FACE,{"disambiguationData":[OSD([subQ3])]}),makeQuery(id+"F3.opExtrude","SWEPT_FACE",FACE,{"disambiguationData":[OSD([sQuery(id+"F2.wireOp",EDGE,"E5.right")])]}),makeQuery(id+"F3.opExtrude","CAP_FACE",FACE,{"disambiguationData":[OSD([sQuery(id+"F2.wireOp",EDGE,"E6.bottom"),subQ1,sQuery(id+"F2.wireOp",EDGE,"E6.left"),subQ0])],"isStart":true}),makeQuery(id+"F3.opExtrude","SWEPT_FACE",FACE,{"disambiguationData":[OSD([subQ1])]}),makeQuery(id+"F3.opExtrude","SWEPT_FACE",FACE,{"disambiguationData":[OSD([subQ0])]}),makeQuery(id+"F3.opExtrude","SWEPT_FACE",FACE,{"disambiguationData":[OSD([sQuery(id+"F2.wireOp",EDGE,"E7.right")])]}),makeQuery(id+"F3.opExtrude","SWEPT_FACE",FACE,{"disambiguationData":[OSD([sQuery(id+"F2.wireOp",EDGE,"E8.right")])]}),makeQuery(id+"F3.opExtrude","SWEPT_FACE",FACE,{"disambiguationData":[OSD([sQuery(id+"F2.wireOp",EDGE,"E9.right")])]}),makeQuery(id+"F3.opExtrude","SWEPT_FACE",FACE,{"disambiguationData":[OSD([sQuery(id+"F2.wireOp",EDGE,"E10.right")])]})])],"derivedFrom":makeQuery(id+"F3.opExtrude","CAP_EDGE",EDGE,{"disambiguationData":[OSD([subQ1])],"isStart":true})});}
            var Q6;
            {var subQ0=sQuery(id+"F2.wireOp",EDGE,"E5.top");var subQ1=sQuery(id+"F2.wireOp",EDGE,"E5.right");var subQ2=sQuery(id+"F0.wireOp",EDGE,"E4.MirrorCS");var subQ3=sQuery(id+"F0.wireOp",EDGE,"E3.MirrorCS");Q6=makeQuery(id+"F4.opBoolean","SPLIT",EDGE,{"disambiguationData":[TD([makeQuery(id+"F1.opExtrude","CAP_FACE",FACE,{"disambiguationData":[OSD([sQuery(id+"F0.wireOp",EDGE,"E1.MirrorCS"),sQuery(id+"F0.wireOp",EDGE,"E2.MirrorCS"),subQ3,subQ2])],"isStart":false}),makeQuery(id+"F1.opExtrude","SWEPT_FACE",FACE,{"disambiguationData":[OSD([subQ3])]}),makeQuery(id+"F1.opExtrude","SWEPT_FACE",FACE,{"disambiguationData":[OSD([subQ2])]}),makeQuery(id+"F3.opExtrude","CAP_FACE",FACE,{"disambiguationData":[OSD([sQuery(id+"F2.wireOp",EDGE,"E5.bottom"),subQ0,sQuery(id+"F2.wireOp",EDGE,"E5.left"),subQ1])],"isStart":true}),makeQuery(id+"F3.opExtrude","SWEPT_FACE",FACE,{"disambiguationData":[OSD([subQ0])]}),makeQuery(id+"F3.opExtrude","SWEPT_FACE",FACE,{"disambiguationData":[OSD([subQ1])]}),makeQuery(id+"F3.opExtrude","SWEPT_FACE",FACE,{"disambiguationData":[OSD([sQuery(id+"F2.wireOp",EDGE,"E6.right")])]}),makeQuery(id+"F3.opExtrude","SWEPT_FACE",FACE,{"disambiguationData":[OSD([sQuery(id+"F2.wireOp",EDGE,"E7.right")])]}),makeQuery(id+"F3.opExtrude","SWEPT_FACE",FACE,{"disambiguationData":[OSD([sQuery(id+"F2.wireOp",EDGE,"E8.right")])]}),makeQuery(id+"F3.opExtrude","SWEPT_FACE",FACE,{"disambiguationData":[OSD([sQuery(id+"F2.wireOp",EDGE,"E9.right")])]}),makeQuery(id+"F3.opExtrude","SWEPT_FACE",FACE,{"disambiguationData":[OSD([sQuery(id+"F2.wireOp",EDGE,"E10.right")])]})])],"derivedFrom":makeQuery(id+"F3.opExtrude","CAP_EDGE",EDGE,{"disambiguationData":[OSD([subQ0])],"isStart":true})});}
            var Q7;
            {var subQ0=sQuery(id+"F2.wireOp",EDGE,"E6.right");var subQ1=sQuery(id+"F2.wireOp",EDGE,"E6.bottom");var subQ2=sQuery(id+"F0.wireOp",EDGE,"E3.MirrorCS");var subQ3=sQuery(id+"F0.wireOp",EDGE,"E4.MirrorCS");Q7=makeQuery(id+"F4.opBoolean","SPLIT",EDGE,{"disambiguationData":[TD([makeQuery(id+"F1.opExtrude","CAP_FACE",FACE,{"disambiguationData":[OSD([sQuery(id+"F0.wireOp",EDGE,"E1.MirrorCS"),sQuery(id+"F0.wireOp",EDGE,"E2.MirrorCS"),subQ2,subQ3])],"isStart":false}),makeQuery(id+"F1.opExtrude","SWEPT_FACE",FACE,{"disambiguationData":[OSD([subQ2])]}),makeQuery(id+"F1.opExtrude","SWEPT_FACE",FACE,{"disambiguationData":[OSD([subQ3])]}),makeQuery(id+"F3.opExtrude","SWEPT_FACE",FACE,{"disambiguationData":[OSD([sQuery(id+"F2.wireOp",EDGE,"E5.right")])]}),makeQuery(id+"F3.opExtrude","SWEPT_FACE",FACE,{"disambiguationData":[OSD([subQ1])]}),makeQuery(id+"F3.opExtrude","CAP_FACE",FACE,{"disambiguationData":[OSD([subQ1,sQuery(id+"F2.wireOp",EDGE,"E6.top"),sQuery(id+"F2.wireOp",EDGE,"E6.left"),subQ0])],"isStart":true}),makeQuery(id+"F3.opExtrude","SWEPT_FACE",FACE,{"disambiguationData":[OSD([subQ0])]}),makeQuery(id+"F3.opExtrude","SWEPT_FACE",FACE,{"disambiguationData":[OSD([sQuery(id+"F2.wireOp",EDGE,"E7.right")])]}),makeQuery(id+"F3.opExtrude","SWEPT_FACE",FACE,{"disambiguationData":[OSD([sQuery(id+"F2.wireOp",EDGE,"E8.right")])]}),makeQuery(id+"F3.opExtrude","SWEPT_FACE",FACE,{"disambiguationData":[OSD([sQuery(id+"F2.wireOp",EDGE,"E9.right")])]}),makeQuery(id+"F3.opExtrude","SWEPT_FACE",FACE,{"disambiguationData":[OSD([sQuery(id+"F2.wireOp",EDGE,"E10.right")])]})])],"derivedFrom":makeQuery(id+"F3.opExtrude","CAP_EDGE",EDGE,{"disambiguationData":[OSD([subQ1])],"isStart":true})});}
            var Q8;
            {var subQ0=sQuery(id+"F2.wireOp",EDGE,"E7.right");var subQ1=sQuery(id+"F2.wireOp",EDGE,"E7.bottom");var subQ2=sQuery(id+"F0.wireOp",EDGE,"E4.MirrorCS");var subQ3=sQuery(id+"F0.wireOp",EDGE,"E3.MirrorCS");Q8=makeQuery(id+"F4.opBoolean","SPLIT",EDGE,{"disambiguationData":[TD([makeQuery(id+"F1.opExtrude","CAP_FACE",FACE,{"disambiguationData":[OSD([sQuery(id+"F0.wireOp",EDGE,"E1.MirrorCS"),sQuery(id+"F0.wireOp",EDGE,"E2.MirrorCS"),subQ3,subQ2])],"isStart":false}),makeQuery(id+"F1.opExtrude","SWEPT_FACE",FACE,{"disambiguationData":[OSD([subQ3])]}),makeQuery(id+"F1.opExtrude","SWEPT_FACE",FACE,{"disambiguationData":[OSD([subQ2])]}),makeQuery(id+"F3.opExtrude","SWEPT_FACE",FACE,{"disambiguationData":[OSD([sQuery(id+"F2.wireOp",EDGE,"E5.right")])]}),makeQuery(id+"F3.opExtrude","SWEPT_FACE",FACE,{"disambiguationData":[OSD([sQuery(id+"F2.wireOp",EDGE,"E6.right")])]}),makeQuery(id+"F3.opExtrude","SWEPT_FACE",FACE,{"disambiguationData":[OSD([subQ1])]}),makeQuery(id+"F3.opExtrude","CAP_FACE",FACE,{"disambiguationData":[OSD([subQ1,sQuery(id+"F2.wireOp",EDGE,"E7.top"),sQuery(id+"F2.wireOp",EDGE,"E7.left"),subQ0])],"isStart":true}),makeQuery(id+"F3.opExtrude","SWEPT_FACE",FACE,{"disambiguationData":[OSD([subQ0])]}),makeQuery(id+"F3.opExtrude","SWEPT_FACE",FACE,{"disambiguationData":[OSD([sQuery(id+"F2.wireOp",EDGE,"E8.right")])]}),makeQuery(id+"F3.opExtrude","SWEPT_FACE",FACE,{"disambiguationData":[OSD([sQuery(id+"F2.wireOp",EDGE,"E9.right")])]}),makeQuery(id+"F3.opExtrude","SWEPT_FACE",FACE,{"disambiguationData":[OSD([sQuery(id+"F2.wireOp",EDGE,"E10.right")])]})])],"derivedFrom":makeQuery(id+"F3.opExtrude","CAP_EDGE",EDGE,{"disambiguationData":[OSD([subQ1])],"isStart":true})});}
            var Q9;
            {var subQ0=sQuery(id+"F2.wireOp",EDGE,"E8.right");var subQ1=sQuery(id+"F2.wireOp",EDGE,"E8.bottom");var subQ2=sQuery(id+"F0.wireOp",EDGE,"E3.MirrorCS");var subQ3=sQuery(id+"F0.wireOp",EDGE,"E4.MirrorCS");Q9=makeQuery(id+"F4.opBoolean","SPLIT",EDGE,{"disambiguationData":[TD([makeQuery(id+"F1.opExtrude","CAP_FACE",FACE,{"disambiguationData":[OSD([sQuery(id+"F0.wireOp",EDGE,"E1.MirrorCS"),sQuery(id+"F0.wireOp",EDGE,"E2.MirrorCS"),subQ2,subQ3])],"isStart":false}),makeQuery(id+"F1.opExtrude","SWEPT_FACE",FACE,{"disambiguationData":[OSD([subQ2])]}),makeQuery(id+"F1.opExtrude","SWEPT_FACE",FACE,{"disambiguationData":[OSD([subQ3])]}),makeQuery(id+"F3.opExtrude","SWEPT_FACE",FACE,{"disambiguationData":[OSD([sQuery(id+"F2.wireOp",EDGE,"E5.right")])]}),makeQuery(id+"F3.opExtrude","SWEPT_FACE",FACE,{"disambiguationData":[OSD([sQuery(id+"F2.wireOp",EDGE,"E6.right")])]}),makeQuery(id+"F3.opExtrude","SWEPT_FACE",FACE,{"disambiguationData":[OSD([sQuery(id+"F2.wireOp",EDGE,"E7.right")])]}),makeQuery(id+"F3.opExtrude","SWEPT_FACE",FACE,{"disambiguationData":[OSD([subQ1])]}),makeQuery(id+"F3.opExtrude","CAP_FACE",FACE,{"disambiguationData":[OSD([subQ1,sQuery(id+"F2.wireOp",EDGE,"E8.top"),sQuery(id+"F2.wireOp",EDGE,"E8.left"),subQ0])],"isStart":true}),makeQuery(id+"F3.opExtrude","SWEPT_FACE",FACE,{"disambiguationData":[OSD([subQ0])]}),makeQuery(id+"F3.opExtrude","SWEPT_FACE",FACE,{"disambiguationData":[OSD([sQuery(id+"F2.wireOp",EDGE,"E9.right")])]}),makeQuery(id+"F3.opExtrude","SWEPT_FACE",FACE,{"disambiguationData":[OSD([sQuery(id+"F2.wireOp",EDGE,"E10.right")])]})])],"derivedFrom":makeQuery(id+"F3.opExtrude","CAP_EDGE",EDGE,{"disambiguationData":[OSD([subQ1])],"isStart":true})});}
            var Q10;
            {var subQ0=sQuery(id+"F2.wireOp",EDGE,"E6.left");var subQ1=sQuery(id+"F2.wireOp",EDGE,"E6.bottom");var subQ2=sQuery(id+"F0.wireOp",EDGE,"E0.right");var subQ3=sQuery(id+"F0.wireOp",EDGE,"E0.left");Q10=makeQuery(id+"F4.opBoolean","SPLIT",EDGE,{"disambiguationData":[TD([makeQuery(id+"F1.opExtrude","CAP_FACE",FACE,{"disambiguationData":[OSD([sQuery(id+"F0.wireOp",EDGE,"E0.bottom"),sQuery(id+"F0.wireOp",EDGE,"E0.top"),subQ3,subQ2])],"isStart":false}),makeQuery(id+"F1.opExtrude","SWEPT_FACE",FACE,{"disambiguationData":[OSD([subQ3])]}),makeQuery(id+"F1.opExtrude","SWEPT_FACE",FACE,{"disambiguationData":[OSD([subQ2])]}),makeQuery(id+"F3.opExtrude","SWEPT_FACE",FACE,{"disambiguationData":[OSD([sQuery(id+"F2.wireOp",EDGE,"E5.left")])]}),makeQuery(id+"F3.opExtrude","SWEPT_FACE",FACE,{"disambiguationData":[OSD([subQ1])]}),makeQuery(id+"F3.opExtrude","CAP_FACE",FACE,{"disambiguationData":[OSD([subQ1,sQuery(id+"F2.wireOp",EDGE,"E6.top"),subQ0,sQuery(id+"F2.wireOp",EDGE,"E6.right")])],"isStart":true}),makeQuery(id+"F3.opExtrude","SWEPT_FACE",FACE,{"disambiguationData":[OSD([subQ0])]}),makeQuery(id+"F3.opExtrude","SWEPT_FACE",FACE,{"disambiguationData":[OSD([sQuery(id+"F2.wireOp",EDGE,"E7.left")])]}),makeQuery(id+"F3.opExtrude","SWEPT_FACE",FACE,{"disambiguationData":[OSD([sQuery(id+"F2.wireOp",EDGE,"E8.left")])]}),makeQuery(id+"F3.opExtrude","SWEPT_FACE",FACE,{"disambiguationData":[OSD([sQuery(id+"F2.wireOp",EDGE,"E9.left")])]}),makeQuery(id+"F3.opExtrude","SWEPT_FACE",FACE,{"disambiguationData":[OSD([sQuery(id+"F2.wireOp",EDGE,"E10.left")])]})])],"derivedFrom":makeQuery(id+"F3.opExtrude","CAP_EDGE",EDGE,{"disambiguationData":[OSD([subQ1])],"isStart":true})});}
            var Q11;
            {var subQ0=sQuery(id+"F2.wireOp",EDGE,"E7.left");var subQ1=sQuery(id+"F2.wireOp",EDGE,"E7.bottom");var subQ2=sQuery(id+"F0.wireOp",EDGE,"E0.right");var subQ3=sQuery(id+"F0.wireOp",EDGE,"E0.left");Q11=makeQuery(id+"F4.opBoolean","SPLIT",EDGE,{"disambiguationData":[TD([makeQuery(id+"F1.opExtrude","CAP_FACE",FACE,{"disambiguationData":[OSD([sQuery(id+"F0.wireOp",EDGE,"E0.bottom"),sQuery(id+"F0.wireOp",EDGE,"E0.top"),subQ3,subQ2])],"isStart":false}),makeQuery(id+"F1.opExtrude","SWEPT_FACE",FACE,{"disambiguationData":[OSD([subQ3])]}),makeQuery(id+"F1.opExtrude","SWEPT_FACE",FACE,{"disambiguationData":[OSD([subQ2])]}),makeQuery(id+"F3.opExtrude","SWEPT_FACE",FACE,{"disambiguationData":[OSD([sQuery(id+"F2.wireOp",EDGE,"E5.left")])]}),makeQuery(id+"F3.opExtrude","SWEPT_FACE",FACE,{"disambiguationData":[OSD([sQuery(id+"F2.wireOp",EDGE,"E6.left")])]}),makeQuery(id+"F3.opExtrude","SWEPT_FACE",FACE,{"disambiguationData":[OSD([subQ1])]}),makeQuery(id+"F3.opExtrude","CAP_FACE",FACE,{"disambiguationData":[OSD([subQ1,sQuery(id+"F2.wireOp",EDGE,"E7.top"),subQ0,sQuery(id+"F2.wireOp",EDGE,"E7.right")])],"isStart":true}),makeQuery(id+"F3.opExtrude","SWEPT_FACE",FACE,{"disambiguationData":[OSD([subQ0])]}),makeQuery(id+"F3.opExtrude","SWEPT_FACE",FACE,{"disambiguationData":[OSD([sQuery(id+"F2.wireOp",EDGE,"E8.left")])]}),makeQuery(id+"F3.opExtrude","SWEPT_FACE",FACE,{"disambiguationData":[OSD([sQuery(id+"F2.wireOp",EDGE,"E9.left")])]}),makeQuery(id+"F3.opExtrude","SWEPT_FACE",FACE,{"disambiguationData":[OSD([sQuery(id+"F2.wireOp",EDGE,"E10.left")])]})])],"derivedFrom":makeQuery(id+"F3.opExtrude","CAP_EDGE",EDGE,{"disambiguationData":[OSD([subQ1])],"isStart":true})});}
            var Q12;
            {var subQ0=sQuery(id+"F2.wireOp",EDGE,"E8.left");var subQ1=sQuery(id+"F2.wireOp",EDGE,"E8.bottom");var subQ2=sQuery(id+"F0.wireOp",EDGE,"E0.right");var subQ3=sQuery(id+"F0.wireOp",EDGE,"E0.left");Q12=makeQuery(id+"F4.opBoolean","SPLIT",EDGE,{"disambiguationData":[TD([makeQuery(id+"F1.opExtrude","CAP_FACE",FACE,{"disambiguationData":[OSD([sQuery(id+"F0.wireOp",EDGE,"E0.bottom"),sQuery(id+"F0.wireOp",EDGE,"E0.top"),subQ3,subQ2])],"isStart":false}),makeQuery(id+"F1.opExtrude","SWEPT_FACE",FACE,{"disambiguationData":[OSD([subQ3])]}),makeQuery(id+"F1.opExtrude","SWEPT_FACE",FACE,{"disambiguationData":[OSD([subQ2])]}),makeQuery(id+"F3.opExtrude","SWEPT_FACE",FACE,{"disambiguationData":[OSD([sQuery(id+"F2.wireOp",EDGE,"E5.left")])]}),makeQuery(id+"F3.opExtrude","SWEPT_FACE",FACE,{"disambiguationData":[OSD([sQuery(id+"F2.wireOp",EDGE,"E6.left")])]}),makeQuery(id+"F3.opExtrude","SWEPT_FACE",FACE,{"disambiguationData":[OSD([sQuery(id+"F2.wireOp",EDGE,"E7.left")])]}),makeQuery(id+"F3.opExtrude","SWEPT_FACE",FACE,{"disambiguationData":[OSD([subQ1])]}),makeQuery(id+"F3.opExtrude","CAP_FACE",FACE,{"disambiguationData":[OSD([subQ1,sQuery(id+"F2.wireOp",EDGE,"E8.top"),subQ0,sQuery(id+"F2.wireOp",EDGE,"E8.right")])],"isStart":true}),makeQuery(id+"F3.opExtrude","SWEPT_FACE",FACE,{"disambiguationData":[OSD([subQ0])]}),makeQuery(id+"F3.opExtrude","SWEPT_FACE",FACE,{"disambiguationData":[OSD([sQuery(id+"F2.wireOp",EDGE,"E9.left")])]}),makeQuery(id+"F3.opExtrude","SWEPT_FACE",FACE,{"disambiguationData":[OSD([sQuery(id+"F2.wireOp",EDGE,"E10.left")])]})])],"derivedFrom":makeQuery(id+"F3.opExtrude","CAP_EDGE",EDGE,{"disambiguationData":[OSD([subQ1])],"isStart":true})});}
            var Q13;
            {var subQ0=sQuery(id+"F2.wireOp",EDGE,"E5.left");var subQ1=sQuery(id+"F0.wireOp",EDGE,"E0.left");var subQ2=sQuery(id+"F2.wireOp",EDGE,"E5.top");var subQ3=sQuery(id+"F0.wireOp",EDGE,"E0.right");Q13=makeQuery(id+"F4.opBoolean","SPLIT",EDGE,{"disambiguationData":[TD([makeQuery(id+"F1.opExtrude","CAP_FACE",FACE,{"disambiguationData":[OSD([sQuery(id+"F0.wireOp",EDGE,"E0.bottom"),sQuery(id+"F0.wireOp",EDGE,"E0.top"),subQ1,subQ3])],"isStart":false}),makeQuery(id+"F1.opExtrude","SWEPT_FACE",FACE,{"disambiguationData":[OSD([subQ1])]}),makeQuery(id+"F1.opExtrude","SWEPT_FACE",FACE,{"disambiguationData":[OSD([subQ3])]}),makeQuery(id+"F3.opExtrude","CAP_FACE",FACE,{"disambiguationData":[OSD([sQuery(id+"F2.wireOp",EDGE,"E5.bottom"),subQ2,subQ0,sQuery(id+"F2.wireOp",EDGE,"E5.right")])],"isStart":true}),makeQuery(id+"F3.opExtrude","SWEPT_FACE",FACE,{"disambiguationData":[OSD([subQ2])]}),makeQuery(id+"F3.opExtrude","SWEPT_FACE",FACE,{"disambiguationData":[OSD([subQ0])]}),makeQuery(id+"F3.opExtrude","SWEPT_FACE",FACE,{"disambiguationData":[OSD([sQuery(id+"F2.wireOp",EDGE,"E6.left")])]}),makeQuery(id+"F3.opExtrude","SWEPT_FACE",FACE,{"disambiguationData":[OSD([sQuery(id+"F2.wireOp",EDGE,"E7.left")])]}),makeQuery(id+"F3.opExtrude","SWEPT_FACE",FACE,{"disambiguationData":[OSD([sQuery(id+"F2.wireOp",EDGE,"E8.left")])]}),makeQuery(id+"F3.opExtrude","SWEPT_FACE",FACE,{"disambiguationData":[OSD([sQuery(id+"F2.wireOp",EDGE,"E9.left")])]}),makeQuery(id+"F3.opExtrude","SWEPT_FACE",FACE,{"disambiguationData":[OSD([sQuery(id+"F2.wireOp",EDGE,"E10.left")])]})])],"derivedFrom":makeQuery(id+"F3.opExtrude","CAP_EDGE",EDGE,{"disambiguationData":[OSD([subQ2])],"isStart":true})});}
            var Q14;
            {var subQ0=sQuery(id+"F2.wireOp",EDGE,"E6.top");var subQ1=sQuery(id+"F2.wireOp",EDGE,"E6.left");var subQ2=sQuery(id+"F0.wireOp",EDGE,"E0.right");var subQ3=sQuery(id+"F0.wireOp",EDGE,"E0.left");Q14=makeQuery(id+"F4.opBoolean","SPLIT",EDGE,{"disambiguationData":[TD([makeQuery(id+"F1.opExtrude","CAP_FACE",FACE,{"disambiguationData":[OSD([sQuery(id+"F0.wireOp",EDGE,"E0.bottom"),sQuery(id+"F0.wireOp",EDGE,"E0.top"),subQ3,subQ2])],"isStart":false}),makeQuery(id+"F1.opExtrude","SWEPT_FACE",FACE,{"disambiguationData":[OSD([subQ3])]}),makeQuery(id+"F1.opExtrude","SWEPT_FACE",FACE,{"disambiguationData":[OSD([subQ2])]}),makeQuery(id+"F3.opExtrude","SWEPT_FACE",FACE,{"disambiguationData":[OSD([sQuery(id+"F2.wireOp",EDGE,"E5.left")])]}),makeQuery(id+"F3.opExtrude","CAP_FACE",FACE,{"disambiguationData":[OSD([sQuery(id+"F2.wireOp",EDGE,"E6.bottom"),subQ0,subQ1,sQuery(id+"F2.wireOp",EDGE,"E6.right")])],"isStart":true}),makeQuery(id+"F3.opExtrude","SWEPT_FACE",FACE,{"disambiguationData":[OSD([subQ0])]}),makeQuery(id+"F3.opExtrude","SWEPT_FACE",FACE,{"disambiguationData":[OSD([subQ1])]}),makeQuery(id+"F3.opExtrude","SWEPT_FACE",FACE,{"disambiguationData":[OSD([sQuery(id+"F2.wireOp",EDGE,"E7.left")])]}),makeQuery(id+"F3.opExtrude","SWEPT_FACE",FACE,{"disambiguationData":[OSD([sQuery(id+"F2.wireOp",EDGE,"E8.left")])]}),makeQuery(id+"F3.opExtrude","SWEPT_FACE",FACE,{"disambiguationData":[OSD([sQuery(id+"F2.wireOp",EDGE,"E9.left")])]}),makeQuery(id+"F3.opExtrude","SWEPT_FACE",FACE,{"disambiguationData":[OSD([sQuery(id+"F2.wireOp",EDGE,"E10.left")])]})])],"derivedFrom":makeQuery(id+"F3.opExtrude","CAP_EDGE",EDGE,{"disambiguationData":[OSD([subQ0])],"isStart":true})});}
            var Q15;
            {var subQ0=sQuery(id+"F2.wireOp",EDGE,"E7.left");var subQ1=sQuery(id+"F2.wireOp",EDGE,"E7.top");var subQ2=sQuery(id+"F0.wireOp",EDGE,"E0.right");var subQ3=sQuery(id+"F0.wireOp",EDGE,"E0.left");Q15=makeQuery(id+"F4.opBoolean","SPLIT",EDGE,{"disambiguationData":[TD([makeQuery(id+"F1.opExtrude","CAP_FACE",FACE,{"disambiguationData":[OSD([sQuery(id+"F0.wireOp",EDGE,"E0.bottom"),sQuery(id+"F0.wireOp",EDGE,"E0.top"),subQ3,subQ2])],"isStart":false}),makeQuery(id+"F1.opExtrude","SWEPT_FACE",FACE,{"disambiguationData":[OSD([subQ3])]}),makeQuery(id+"F1.opExtrude","SWEPT_FACE",FACE,{"disambiguationData":[OSD([subQ2])]}),makeQuery(id+"F3.opExtrude","SWEPT_FACE",FACE,{"disambiguationData":[OSD([sQuery(id+"F2.wireOp",EDGE,"E5.left")])]}),makeQuery(id+"F3.opExtrude","SWEPT_FACE",FACE,{"disambiguationData":[OSD([sQuery(id+"F2.wireOp",EDGE,"E6.left")])]}),makeQuery(id+"F3.opExtrude","CAP_FACE",FACE,{"disambiguationData":[OSD([sQuery(id+"F2.wireOp",EDGE,"E7.bottom"),subQ1,subQ0,sQuery(id+"F2.wireOp",EDGE,"E7.right")])],"isStart":true}),makeQuery(id+"F3.opExtrude","SWEPT_FACE",FACE,{"disambiguationData":[OSD([subQ1])]}),makeQuery(id+"F3.opExtrude","SWEPT_FACE",FACE,{"disambiguationData":[OSD([subQ0])]}),makeQuery(id+"F3.opExtrude","SWEPT_FACE",FACE,{"disambiguationData":[OSD([sQuery(id+"F2.wireOp",EDGE,"E8.left")])]}),makeQuery(id+"F3.opExtrude","SWEPT_FACE",FACE,{"disambiguationData":[OSD([sQuery(id+"F2.wireOp",EDGE,"E9.left")])]}),makeQuery(id+"F3.opExtrude","SWEPT_FACE",FACE,{"disambiguationData":[OSD([sQuery(id+"F2.wireOp",EDGE,"E10.left")])]})])],"derivedFrom":makeQuery(id+"F3.opExtrude","CAP_EDGE",EDGE,{"disambiguationData":[OSD([subQ1])],"isStart":true})});}
            var Q16;
            {var subQ0=sQuery(id+"F2.wireOp",EDGE,"E8.left");var subQ1=sQuery(id+"F2.wireOp",EDGE,"E8.top");var subQ2=sQuery(id+"F0.wireOp",EDGE,"E0.right");var subQ3=sQuery(id+"F0.wireOp",EDGE,"E0.left");Q16=makeQuery(id+"F4.opBoolean","SPLIT",EDGE,{"disambiguationData":[TD([makeQuery(id+"F1.opExtrude","CAP_FACE",FACE,{"disambiguationData":[OSD([sQuery(id+"F0.wireOp",EDGE,"E0.bottom"),sQuery(id+"F0.wireOp",EDGE,"E0.top"),subQ3,subQ2])],"isStart":false}),makeQuery(id+"F1.opExtrude","SWEPT_FACE",FACE,{"disambiguationData":[OSD([subQ3])]}),makeQuery(id+"F1.opExtrude","SWEPT_FACE",FACE,{"disambiguationData":[OSD([subQ2])]}),makeQuery(id+"F3.opExtrude","SWEPT_FACE",FACE,{"disambiguationData":[OSD([sQuery(id+"F2.wireOp",EDGE,"E5.left")])]}),makeQuery(id+"F3.opExtrude","SWEPT_FACE",FACE,{"disambiguationData":[OSD([sQuery(id+"F2.wireOp",EDGE,"E6.left")])]}),makeQuery(id+"F3.opExtrude","SWEPT_FACE",FACE,{"disambiguationData":[OSD([sQuery(id+"F2.wireOp",EDGE,"E7.left")])]}),makeQuery(id+"F3.opExtrude","CAP_FACE",FACE,{"disambiguationData":[OSD([sQuery(id+"F2.wireOp",EDGE,"E8.bottom"),subQ1,subQ0,sQuery(id+"F2.wireOp",EDGE,"E8.right")])],"isStart":true}),makeQuery(id+"F3.opExtrude","SWEPT_FACE",FACE,{"disambiguationData":[OSD([subQ1])]}),makeQuery(id+"F3.opExtrude","SWEPT_FACE",FACE,{"disambiguationData":[OSD([subQ0])]}),makeQuery(id+"F3.opExtrude","SWEPT_FACE",FACE,{"disambiguationData":[OSD([sQuery(id+"F2.wireOp",EDGE,"E9.left")])]}),makeQuery(id+"F3.opExtrude","SWEPT_FACE",FACE,{"disambiguationData":[OSD([sQuery(id+"F2.wireOp",EDGE,"E10.left")])]})])],"derivedFrom":makeQuery(id+"F3.opExtrude","CAP_EDGE",EDGE,{"disambiguationData":[OSD([subQ1])],"isStart":true})});}
            var Q17;
            {var subQ0=sQuery(id+"F2.wireOp",EDGE,"E9.left");var subQ1=sQuery(id+"F2.wireOp",EDGE,"E9.top");var subQ2=sQuery(id+"F0.wireOp",EDGE,"E0.right");var subQ3=sQuery(id+"F0.wireOp",EDGE,"E0.left");Q17=makeQuery(id+"F4.opBoolean","SPLIT",EDGE,{"disambiguationData":[TD([makeQuery(id+"F1.opExtrude","CAP_FACE",FACE,{"disambiguationData":[OSD([sQuery(id+"F0.wireOp",EDGE,"E0.bottom"),sQuery(id+"F0.wireOp",EDGE,"E0.top"),subQ3,subQ2])],"isStart":false}),makeQuery(id+"F1.opExtrude","SWEPT_FACE",FACE,{"disambiguationData":[OSD([subQ3])]}),makeQuery(id+"F1.opExtrude","SWEPT_FACE",FACE,{"disambiguationData":[OSD([subQ2])]}),makeQuery(id+"F3.opExtrude","SWEPT_FACE",FACE,{"disambiguationData":[OSD([sQuery(id+"F2.wireOp",EDGE,"E5.left")])]}),makeQuery(id+"F3.opExtrude","SWEPT_FACE",FACE,{"disambiguationData":[OSD([sQuery(id+"F2.wireOp",EDGE,"E6.left")])]}),makeQuery(id+"F3.opExtrude","SWEPT_FACE",FACE,{"disambiguationData":[OSD([sQuery(id+"F2.wireOp",EDGE,"E7.left")])]}),makeQuery(id+"F3.opExtrude","SWEPT_FACE",FACE,{"disambiguationData":[OSD([sQuery(id+"F2.wireOp",EDGE,"E8.left")])]}),makeQuery(id+"F3.opExtrude","CAP_FACE",FACE,{"disambiguationData":[OSD([sQuery(id+"F2.wireOp",EDGE,"E9.bottom"),subQ1,subQ0,sQuery(id+"F2.wireOp",EDGE,"E9.right")])],"isStart":true}),makeQuery(id+"F3.opExtrude","SWEPT_FACE",FACE,{"disambiguationData":[OSD([subQ1])]}),makeQuery(id+"F3.opExtrude","SWEPT_FACE",FACE,{"disambiguationData":[OSD([subQ0])]}),makeQuery(id+"F3.opExtrude","SWEPT_FACE",FACE,{"disambiguationData":[OSD([sQuery(id+"F2.wireOp",EDGE,"E10.left")])]})])],"derivedFrom":makeQuery(id+"F3.opExtrude","CAP_EDGE",EDGE,{"disambiguationData":[OSD([subQ1])],"isStart":true})});}
            var Q18;
            {var subQ0=sQuery(id+"F2.wireOp",EDGE,"E10.left");var subQ1=sQuery(id+"F2.wireOp",EDGE,"E10.bottom");var subQ2=sQuery(id+"F0.wireOp",EDGE,"E0.right");var subQ3=sQuery(id+"F0.wireOp",EDGE,"E0.left");Q18=makeQuery(id+"F4.opBoolean","SPLIT",EDGE,{"disambiguationData":[TD([makeQuery(id+"F1.opExtrude","CAP_FACE",FACE,{"disambiguationData":[OSD([sQuery(id+"F0.wireOp",EDGE,"E0.bottom"),sQuery(id+"F0.wireOp",EDGE,"E0.top"),subQ3,subQ2])],"isStart":false}),makeQuery(id+"F1.opExtrude","SWEPT_FACE",FACE,{"disambiguationData":[OSD([subQ3])]}),makeQuery(id+"F1.opExtrude","SWEPT_FACE",FACE,{"disambiguationData":[OSD([subQ2])]}),makeQuery(id+"F3.opExtrude","SWEPT_FACE",FACE,{"disambiguationData":[OSD([sQuery(id+"F2.wireOp",EDGE,"E5.left")])]}),makeQuery(id+"F3.opExtrude","SWEPT_FACE",FACE,{"disambiguationData":[OSD([sQuery(id+"F2.wireOp",EDGE,"E6.left")])]}),makeQuery(id+"F3.opExtrude","SWEPT_FACE",FACE,{"disambiguationData":[OSD([sQuery(id+"F2.wireOp",EDGE,"E7.left")])]}),makeQuery(id+"F3.opExtrude","SWEPT_FACE",FACE,{"disambiguationData":[OSD([sQuery(id+"F2.wireOp",EDGE,"E8.left")])]}),makeQuery(id+"F3.opExtrude","SWEPT_FACE",FACE,{"disambiguationData":[OSD([sQuery(id+"F2.wireOp",EDGE,"E9.left")])]}),makeQuery(id+"F3.opExtrude","SWEPT_FACE",FACE,{"disambiguationData":[OSD([subQ1])]}),makeQuery(id+"F3.opExtrude","CAP_FACE",FACE,{"disambiguationData":[OSD([subQ1,sQuery(id+"F2.wireOp",EDGE,"E10.top"),subQ0,sQuery(id+"F2.wireOp",EDGE,"E10.right")])],"isStart":true}),makeQuery(id+"F3.opExtrude","SWEPT_FACE",FACE,{"disambiguationData":[OSD([subQ0])]})])],"derivedFrom":makeQuery(id+"F3.opExtrude","CAP_EDGE",EDGE,{"disambiguationData":[OSD([subQ1])],"isStart":true})});}
            var Q19;
            {var subQ0=sQuery(id+"F2.wireOp",EDGE,"E9.left");var subQ1=sQuery(id+"F2.wireOp",EDGE,"E9.bottom");var subQ2=sQuery(id+"F0.wireOp",EDGE,"E0.right");var subQ3=sQuery(id+"F0.wireOp",EDGE,"E0.left");Q19=makeQuery(id+"F4.opBoolean","SPLIT",EDGE,{"disambiguationData":[TD([makeQuery(id+"F1.opExtrude","CAP_FACE",FACE,{"disambiguationData":[OSD([sQuery(id+"F0.wireOp",EDGE,"E0.bottom"),sQuery(id+"F0.wireOp",EDGE,"E0.top"),subQ3,subQ2])],"isStart":false}),makeQuery(id+"F1.opExtrude","SWEPT_FACE",FACE,{"disambiguationData":[OSD([subQ3])]}),makeQuery(id+"F1.opExtrude","SWEPT_FACE",FACE,{"disambiguationData":[OSD([subQ2])]}),makeQuery(id+"F3.opExtrude","SWEPT_FACE",FACE,{"disambiguationData":[OSD([sQuery(id+"F2.wireOp",EDGE,"E5.left")])]}),makeQuery(id+"F3.opExtrude","SWEPT_FACE",FACE,{"disambiguationData":[OSD([sQuery(id+"F2.wireOp",EDGE,"E6.left")])]}),makeQuery(id+"F3.opExtrude","SWEPT_FACE",FACE,{"disambiguationData":[OSD([sQuery(id+"F2.wireOp",EDGE,"E7.left")])]}),makeQuery(id+"F3.opExtrude","SWEPT_FACE",FACE,{"disambiguationData":[OSD([sQuery(id+"F2.wireOp",EDGE,"E8.left")])]}),makeQuery(id+"F3.opExtrude","SWEPT_FACE",FACE,{"disambiguationData":[OSD([subQ1])]}),makeQuery(id+"F3.opExtrude","CAP_FACE",FACE,{"disambiguationData":[OSD([subQ1,sQuery(id+"F2.wireOp",EDGE,"E9.top"),subQ0,sQuery(id+"F2.wireOp",EDGE,"E9.right")])],"isStart":true}),makeQuery(id+"F3.opExtrude","SWEPT_FACE",FACE,{"disambiguationData":[OSD([subQ0])]}),makeQuery(id+"F3.opExtrude","SWEPT_FACE",FACE,{"disambiguationData":[OSD([sQuery(id+"F2.wireOp",EDGE,"E10.left")])]})])],"derivedFrom":makeQuery(id+"F3.opExtrude","CAP_EDGE",EDGE,{"disambiguationData":[OSD([subQ1])],"isStart":true})});}
            fillet(context, id + "F17", {"entities" : qUnion([Q0, Q1, Q2, Q3, Q4, Q5, Q6, Q7, Q8, Q9, Q10, Q11, Q12, Q13, Q14, Q15, Q16, Q17, Q18, Q19]), "radius" : 1 * mm, "tangentPropagation" : true, "allowEdgeOverflow" : false});
        }
        {
            var Q0;
            {var subQ2=sQuery(id+"F13.wireOp",EDGE,"E15.right");Q0=makeQuery(id+"F14.boolean.opBoolean","COPY",FACE,{"disambiguationData":[TD([makeQuery(id+"F1.opExtrude","SWEPT_FACE",FACE,{"disambiguationData":[OSD([sQuery(id+"F0.wireOp",EDGE,"E0.top")])]})])],"derivedFrom":makeQuery(id+"F14.opExtrude","SWEPT_FACE",FACE,{"disambiguationData":[OSD([subQ2])]})});}
            var Q1;
            {var subQ0=sQuery(id+"F2.wireOp",EDGE,"E9.bottom");var subQ2=sQuery(id+"F13.wireOp",EDGE,"E15.right");Q1=makeQuery(id+"F14.boolean.opBoolean","COPY",FACE,{"disambiguationData":[TD([makeQuery(id+"F3.opExtrude","SWEPT_FACE",FACE,{"disambiguationData":[OSD([subQ0])]})])],"derivedFrom":makeQuery(id+"F14.opExtrude","SWEPT_FACE",FACE,{"disambiguationData":[OSD([subQ2])]})});}
            var Q2;
            {var subQ0=sQuery(id+"F2.wireOp",EDGE,"E8.bottom");var subQ2=sQuery(id+"F13.wireOp",EDGE,"E15.right");Q2=makeQuery(id+"F14.boolean.opBoolean","COPY",FACE,{"disambiguationData":[TD([makeQuery(id+"F3.opExtrude","SWEPT_FACE",FACE,{"disambiguationData":[OSD([subQ0])]})])],"derivedFrom":makeQuery(id+"F14.opExtrude","SWEPT_FACE",FACE,{"disambiguationData":[OSD([subQ2])]})});}
            var Q3;
            {var subQ0=sQuery(id+"F2.wireOp",EDGE,"E7.bottom");var subQ2=sQuery(id+"F13.wireOp",EDGE,"E15.right");Q3=makeQuery(id+"F14.boolean.opBoolean","COPY",FACE,{"disambiguationData":[TD([makeQuery(id+"F3.opExtrude","SWEPT_FACE",FACE,{"disambiguationData":[OSD([subQ0])]})])],"derivedFrom":makeQuery(id+"F14.opExtrude","SWEPT_FACE",FACE,{"disambiguationData":[OSD([subQ2])]})});}
            var Q4;
            {var subQ0=sQuery(id+"F2.wireOp",EDGE,"E6.bottom");var subQ2=sQuery(id+"F13.wireOp",EDGE,"E15.right");Q4=makeQuery(id+"F14.boolean.opBoolean","COPY",FACE,{"disambiguationData":[TD([makeQuery(id+"F3.opExtrude","SWEPT_FACE",FACE,{"disambiguationData":[OSD([subQ0])]})])],"derivedFrom":makeQuery(id+"F14.opExtrude","SWEPT_FACE",FACE,{"disambiguationData":[OSD([subQ2])]})});}
            var Q5;
            {var subQ0=sQuery(id+"F2.wireOp",EDGE,"E6.bottom");var subQ2=sQuery(id+"F13.wireOp",EDGE,"E16.right");Q5=makeQuery(id+"F14.boolean.opBoolean","COPY",FACE,{"disambiguationData":[TD([makeQuery(id+"F3.opExtrude","SWEPT_FACE",FACE,{"disambiguationData":[OSD([subQ0])]})])],"derivedFrom":makeQuery(id+"F14.opExtrude","SWEPT_FACE",FACE,{"disambiguationData":[OSD([subQ2])]})});}
            var Q6;
            {var subQ0=sQuery(id+"F2.wireOp",EDGE,"E7.bottom");var subQ2=sQuery(id+"F13.wireOp",EDGE,"E16.right");Q6=makeQuery(id+"F14.boolean.opBoolean","COPY",FACE,{"disambiguationData":[TD([makeQuery(id+"F3.opExtrude","SWEPT_FACE",FACE,{"disambiguationData":[OSD([subQ0])]})])],"derivedFrom":makeQuery(id+"F14.opExtrude","SWEPT_FACE",FACE,{"disambiguationData":[OSD([subQ2])]})});}
            var Q7;
            {var subQ0=sQuery(id+"F2.wireOp",EDGE,"E8.bottom");var subQ2=sQuery(id+"F13.wireOp",EDGE,"E16.right");Q7=makeQuery(id+"F14.boolean.opBoolean","COPY",FACE,{"disambiguationData":[TD([makeQuery(id+"F3.opExtrude","SWEPT_FACE",FACE,{"disambiguationData":[OSD([subQ0])]})])],"derivedFrom":makeQuery(id+"F14.opExtrude","SWEPT_FACE",FACE,{"disambiguationData":[OSD([subQ2])]})});}
            var Q8;
            {var subQ0=sQuery(id+"F2.wireOp",EDGE,"E9.bottom");var subQ2=sQuery(id+"F13.wireOp",EDGE,"E16.right");Q8=makeQuery(id+"F14.boolean.opBoolean","COPY",FACE,{"disambiguationData":[TD([makeQuery(id+"F3.opExtrude","SWEPT_FACE",FACE,{"disambiguationData":[OSD([subQ0])]})])],"derivedFrom":makeQuery(id+"F14.opExtrude","SWEPT_FACE",FACE,{"disambiguationData":[OSD([subQ2])]})});}
            var Q9;
            {var subQ2=sQuery(id+"F13.wireOp",EDGE,"E16.right");Q9=makeQuery(id+"F14.boolean.opBoolean","COPY",FACE,{"disambiguationData":[TD([makeQuery(id+"F1.opExtrude","SWEPT_FACE",FACE,{"disambiguationData":[OSD([sQuery(id+"F0.wireOp",EDGE,"E0.top")])]})])],"derivedFrom":makeQuery(id+"F14.opExtrude","SWEPT_FACE",FACE,{"disambiguationData":[OSD([subQ2])]})});}
            fillet(context, id + "F18", {"entities" : qUnion([Q0, Q1, Q2, Q3, Q4, Q5, Q6, Q7, Q8, Q9]), "radius" : .5 * mm, "tangentPropagation" : true, "allowEdgeOverflow" : false});
        }
    });
